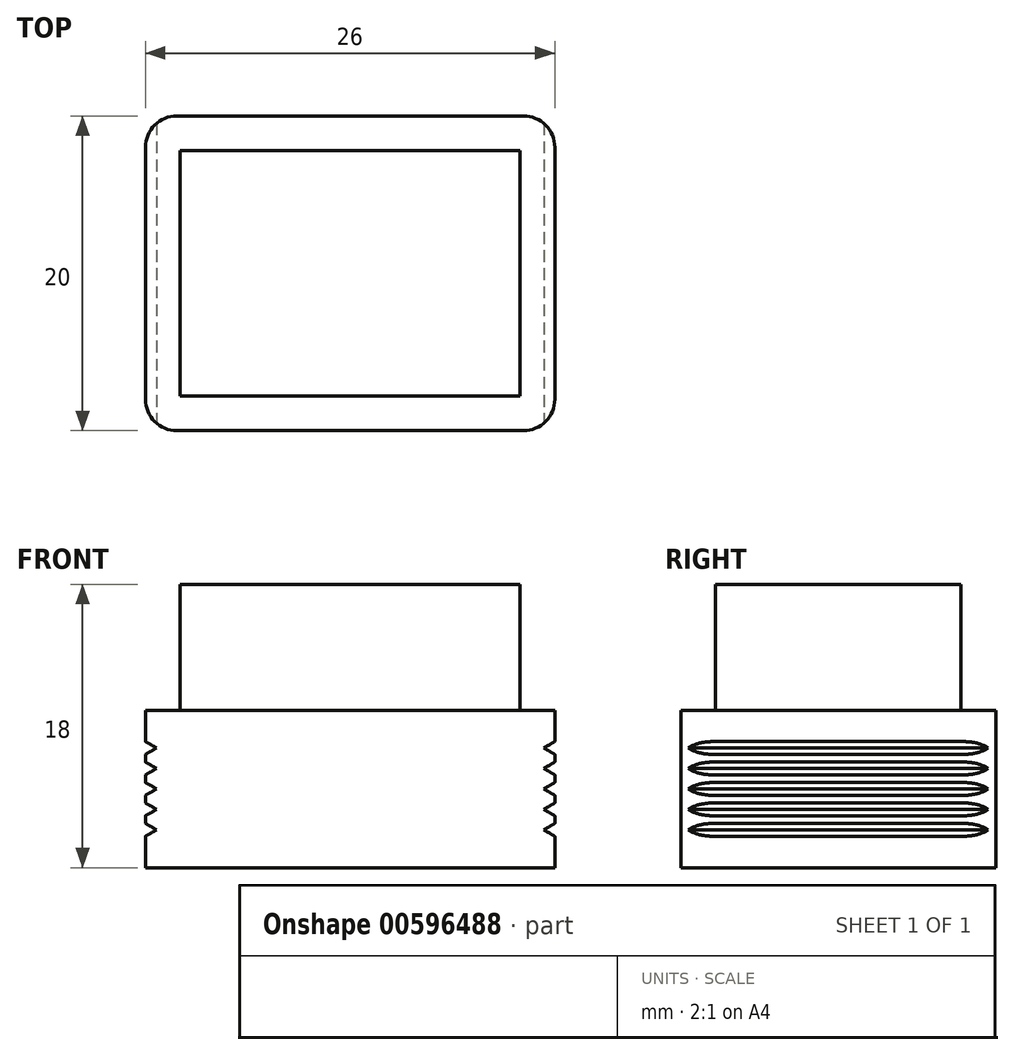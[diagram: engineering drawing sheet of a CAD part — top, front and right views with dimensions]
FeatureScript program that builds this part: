
annotation { "Feature Type Name" : "Feature", "Feature Type Description" : "" }
export const myFeature = defineFeature(function(context is Context, id is Id, definition is map)
    precondition{}
    {
        {
            var Q0;
            Q0=qCreatedBy(makeId("Top.planeOp"),FACE);
            var sketch = newSketch(context, id + "F0", { "sketchPlane" : qUnion([Q0])});
            skLineSegment(sketch, "E0.bottom", {"start": v(0, 0) * mm, "end": v(26, 0) * mm});
            skLineSegment(sketch, "E0.top", {"start": v(0, 20) * mm, "end": v(26, 20) * mm});
            skLineSegment(sketch, "E0.left", {"start": v(0, 0) * mm, "end": v(0, 20) * mm});
            skLineSegment(sketch, "E0.right", {"start": v(26, 0) * mm, "end": v(26, 20) * mm});
            skLineSegment(sketch, "E1.bottom", {"start": v(23.8, 17.8) * mm, "end": v(2.2, 17.8) * mm});
            skLineSegment(sketch, "E1.top", {"start": v(23.8, 2.2) * mm, "end": v(2.2, 2.2) * mm});
            skLineSegment(sketch, "E1.left", {"start": v(23.8, 17.8) * mm, "end": v(23.8, 2.2) * mm});
            skLineSegment(sketch, "E1.right", {"start": v(2.2, 17.8) * mm, "end": v(2.2, 2.2) * mm});
            skPoint(sketch, "E1.middle", {"position": v(13, 10) * mm});
            skPoint(sketch, "E1.middle.positionSnap0", {"position": v(13, 20) * mm});
            skPoint(sketch, "E1.middle.positionSnap1", {"position": v(0, 10) * mm});
            skPoint(sketch, "E1.centerSnap0", {"position": v(13, 20) * mm});
            skPoint(sketch, "E1.centerSnap1", {"position": v(0, 10) * mm});
            skSolve(sketch);
        }
        {
            var Q0;
            Q0=makeQuery(id+"F0.imprint","IMPRINT",FACE,{"disambiguationData":[TD([[makeQuery(id+"F0.imprint","IMPRINT",EDGE,{"derivedFrom":sQuery(id+"F0.wireOp",EDGE,"E0.bottom")}),1.0]])]});
            extrude(context, id + "F1", {"entities" : qUnion([Q0]), "depth" : 10 * mm, "offsetDistance" : 25 * mm});
        }
        {
            var Q0;
            Q0=makeQuery(id+"F0.imprint","IMPRINT",FACE,{"disambiguationData":[TD([[makeQuery(id+"F0.imprint","IMPRINT",EDGE,{"derivedFrom":sQuery(id+"F0.wireOp",EDGE,"E1.bottom")}),1.0]])]});
            extrude(context, id + "F2", {"entities" : qUnion([Q0]), "operationType" : NewBodyOperationType.ADD, "depth" : 18 * mm, "offsetDistance" : 25 * mm});
        }
        {
            var Q0;
            Q0=makeQuery(id+"F1.opExtrude","SWEPT_EDGE",EDGE,{"disambiguationData":[OSD([sQuery(id+"F0.wireOp",EDGE,"E0.bottom"),sQuery(id+"F0.wireOp",EDGE,"E0.right")])]});
            var Q1;
            Q1=makeQuery(id+"F1.opExtrude","SWEPT_EDGE",EDGE,{"disambiguationData":[OSD([sQuery(id+"F0.wireOp",EDGE,"E0.top"),sQuery(id+"F0.wireOp",EDGE,"E0.right")])]});
            var Q2;
            Q2=makeQuery(id+"F1.opExtrude","SWEPT_EDGE",EDGE,{"disambiguationData":[OSD([sQuery(id+"F0.wireOp",EDGE,"E0.top"),sQuery(id+"F0.wireOp",EDGE,"E0.left")])]});
            var Q3;
            Q3=makeQuery(id+"F1.opExtrude","SWEPT_EDGE",EDGE,{"disambiguationData":[OSD([sQuery(id+"F0.wireOp",EDGE,"E0.bottom"),sQuery(id+"F0.wireOp",EDGE,"E0.left")])]});
            fillet(context, id + "F3", {"entities" : qUnion([Q0, Q1, Q2, Q3]), "radius" : 2 * mm, "tangentPropagation" : true, "allowEdgeOverflow" : false});
        }
        {
            var Q0;
            Q0=makeQuery(id+"F1.opExtrude","SWEPT_FACE",FACE,{"disambiguationData":[OSD([sQuery(id+"F0.wireOp",EDGE,"E0.bottom")])]});
            var sketch = newSketch(context, id + "F4", { "sketchPlane" : qUnion([Q0])});
            skLineSegment(sketch, "E2.0", {"start": v(0, 0) * mm, "end": v(0, 10) * mm});
            skLineSegment(sketch, "E3.0", {"start": v(26, 10) * mm, "end": v(26, 0) * mm});
            skLineSegment(sketch, "E4", {"start": v(0, 5) * mm, "end": v(26, 5) * mm, "construction": true});
            skLineSegment(sketch, "E5", {"start": v(13, 10) * mm, "end": v(13, 0) * mm, "construction": true});
            skCircle(sketch, "E6.cCircle", {"center": v(0, 5) * mm, "radius": 0.35 * mm, "construction": true});
            skLineSegment(sketch, "E6.0", {"start": v(-0.35, 4.4) * mm, "end": v(-0.35, 5.6) * mm});
            skLineSegment(sketch, "E6.1", {"start": v(-0.35, 5.6) * mm, "end": v(0.7, 5) * mm});
            skLineSegment(sketch, "E6.2", {"start": v(0.7, 5) * mm, "end": v(-0.35, 4.4) * mm});
            skPoint(sketch, "E6.0.midPoint", {"position": v(-0.35, 5) * mm});
            skPoint(sketch, "E7.0.1.0", {"position": v(-0.35, 6.3) * mm});
            skLineSegment(sketch, "E7.0.1.1", {"start": v(0.7, 6.3) * mm, "end": v(-0.35, 5.7) * mm});
            skLineSegment(sketch, "E7.0.1.2", {"start": v(-0.35, 6.9) * mm, "end": v(0.7, 6.3) * mm});
            skLineSegment(sketch, "E7.0.1.3", {"start": v(-0.35, 5.7) * mm, "end": v(-0.35, 6.9) * mm});
            skCircle(sketch, "E7.0.1.4", {"center": v(0, 6.3) * mm, "radius": 0.35 * mm, "construction": true});
            skPoint(sketch, "E7.0.2.0", {"position": v(-0.35, 7.6) * mm});
            skLineSegment(sketch, "E7.0.2.1", {"start": v(0.7, 7.6) * mm, "end": v(-0.35, 7) * mm});
            skLineSegment(sketch, "E7.0.2.2", {"start": v(-0.35, 8.2) * mm, "end": v(0.7, 7.6) * mm});
            skLineSegment(sketch, "E7.0.2.3", {"start": v(-0.35, 7) * mm, "end": v(-0.35, 8.2) * mm});
            skCircle(sketch, "E7.0.2.4", {"center": v(0, 7.6) * mm, "radius": 0.35 * mm, "construction": true});
            skLineSegment(sketch, "E7.direction1", {"start": v(-0.35, 5) * mm, "end": v(3.53, 5) * mm, "construction": true});
            skLineSegment(sketch, "E7.direction2", {"start": v(-0.35, 5) * mm, "end": v(-0.35, 6.3) * mm, "construction": true});
            skLineSegment(sketch, "E8.MirrorCS", {"start": v(0.7, 2.4) * mm, "end": v(-0.35, 3) * mm});
            skCircle(sketch, "E9.MirrorC", {"center": v(0, 3.7) * mm, "radius": 0.35 * mm, "construction": true});
            skPoint(sketch, "E10.MirrorP", {"position": v(-0.35, 2.4) * mm});
            skCircle(sketch, "E11.MirrorC", {"center": v(0, 2.4) * mm, "radius": 0.35 * mm, "construction": true});
            skLineSegment(sketch, "E12.MirrorCS", {"start": v(-0.35, 3) * mm, "end": v(-0.35, 1.8) * mm});
            skLineSegment(sketch, "E13.MirrorCS", {"start": v(-0.35, 1.8) * mm, "end": v(0.7, 2.4) * mm});
            skLineSegment(sketch, "E14.MirrorCS", {"start": v(0.7, 3.7) * mm, "end": v(-0.35, 4.3) * mm});
            skLineSegment(sketch, "E15.MirrorCS", {"start": v(-0.35, 4.3) * mm, "end": v(-0.35, 3.1) * mm});
            skLineSegment(sketch, "E16.MirrorCS", {"start": v(-0.35, 3.1) * mm, "end": v(0.7, 3.7) * mm});
            skPoint(sketch, "E17.MirrorP", {"position": v(-0.35, 3.7) * mm});
            skLineSegment(sketch, "E18.MirrorCS", {"start": v(-0.35, 5.6) * mm, "end": v(-0.35, 4.4) * mm});
            skLineSegment(sketch, "E19.MirrorCS", {"start": v(-0.35, 5) * mm, "end": v(-0.35, 3.7) * mm, "construction": true});
            skLineSegment(sketch, "E20.MirrorCS", {"start": v(0.7, 5) * mm, "end": v(-0.35, 5.6) * mm});
            skLineSegment(sketch, "E21.MirrorCS", {"start": v(-0.35, 4.4) * mm, "end": v(0.7, 5) * mm});
            skLineSegment(sketch, "E22.MirrorCS", {"start": v(26.35, 5.6) * mm, "end": v(26.35, 4.4) * mm});
            skLineSegment(sketch, "E23.MirrorCS", {"start": v(26.35, 4.4) * mm, "end": v(26.35, 5.6) * mm});
            skLineSegment(sketch, "E24.MirrorCS", {"start": v(26.35, 3) * mm, "end": v(26.35, 1.8) * mm});
            skLineSegment(sketch, "E25.MirrorCS", {"start": v(26.35, 4.3) * mm, "end": v(26.35, 3.1) * mm});
            skLineSegment(sketch, "E26.MirrorCS", {"start": v(26.35, 5.7) * mm, "end": v(26.35, 6.9) * mm});
            skLineSegment(sketch, "E27.MirrorCS", {"start": v(26.35, 5) * mm, "end": v(26.35, 6.3) * mm, "construction": true});
            skLineSegment(sketch, "E28.MirrorCS", {"start": v(26.35, 7) * mm, "end": v(26.35, 8.2) * mm});
            skLineSegment(sketch, "E29.MirrorCS", {"start": v(26.35, 5) * mm, "end": v(26.35, 3.7) * mm, "construction": true});
            skLineSegment(sketch, "E30.MirrorCS", {"start": v(25.3, 6.3) * mm, "end": v(26.35, 5.7) * mm});
            skCircle(sketch, "E31.MirrorC", {"center": v(26, 2.4) * mm, "radius": 0.35 * mm, "construction": true});
            skPoint(sketch, "E32.MirrorP", {"position": v(26.35, 6.3) * mm});
            skPoint(sketch, "E33.MirrorP", {"position": v(26.35, 5) * mm});
            skPoint(sketch, "E34.MirrorP", {"position": v(26.35, 2.4) * mm});
            skCircle(sketch, "E35.MirrorC", {"center": v(26, 7.6) * mm, "radius": 0.35 * mm, "construction": true});
            skLineSegment(sketch, "E36.MirrorCS", {"start": v(26.35, 4.4) * mm, "end": v(25.3, 5) * mm});
            skLineSegment(sketch, "E37.MirrorCS", {"start": v(25.3, 2.4) * mm, "end": v(26.35, 3) * mm});
            skLineSegment(sketch, "E38.MirrorCS", {"start": v(25.3, 3.7) * mm, "end": v(26.35, 4.3) * mm});
            skCircle(sketch, "E39.MirrorC", {"center": v(26, 6.3) * mm, "radius": 0.35 * mm, "construction": true});
            skCircle(sketch, "E40.MirrorC", {"center": v(26, 5) * mm, "radius": 0.35 * mm, "construction": true});
            skLineSegment(sketch, "E41.MirrorCS", {"start": v(26.35, 1.8) * mm, "end": v(25.3, 2.4) * mm});
            skCircle(sketch, "E42.MirrorC", {"center": v(26, 3.7) * mm, "radius": 0.35 * mm, "construction": true});
            skPoint(sketch, "E43.MirrorP", {"position": v(26.35, 3.7) * mm});
            skLineSegment(sketch, "E44.MirrorCS", {"start": v(25.3, 7.6) * mm, "end": v(26.35, 7) * mm});
            skLineSegment(sketch, "E45.MirrorCS", {"start": v(26.35, 3.1) * mm, "end": v(25.3, 3.7) * mm});
            skPoint(sketch, "E46.MirrorP", {"position": v(26.35, 7.6) * mm});
            skLineSegment(sketch, "E47.MirrorCS", {"start": v(26.35, 6.9) * mm, "end": v(25.3, 6.3) * mm});
            skLineSegment(sketch, "E48.MirrorCS", {"start": v(25.3, 5) * mm, "end": v(26.35, 5.6) * mm});
            skLineSegment(sketch, "E49.MirrorCS", {"start": v(26.35, 5.6) * mm, "end": v(25.3, 5) * mm});
            skLineSegment(sketch, "E50.MirrorCS", {"start": v(25.3, 5) * mm, "end": v(26.35, 4.4) * mm});
            skLineSegment(sketch, "E51.MirrorCS", {"start": v(26.35, 8.2) * mm, "end": v(25.3, 7.6) * mm});
            skSolve(sketch);
        }
        {
            var Q0;
            {var subQ0=sQuery(id+"F4.wireOp",EDGE,"E37.MirrorCS");var subQ1=sQuery(id+"F4.wireOp",EDGE,"E3.0");var subQ2=makeQuery(id+"F4.imprint","INTERSECT",VERTEX,{"derivedFrom":[subQ1,subQ0]});Q0=makeQuery(id+"F4.imprint","IMPRINT",FACE,{"disambiguationData":[TD([[makeQuery(id+"F4.imprint","IMPRINT",EDGE,{"disambiguationData":[TD([[subQ2,-1.0]])],"derivedFrom":subQ1}),-1.0]])]});}
            var Q1;
            {var subQ0=sQuery(id+"F4.wireOp",EDGE,"E38.MirrorCS");var subQ1=sQuery(id+"F4.wireOp",EDGE,"E3.0");var subQ2=makeQuery(id+"F4.imprint","INTERSECT",VERTEX,{"derivedFrom":[subQ1,subQ0]});Q1=makeQuery(id+"F4.imprint","IMPRINT",FACE,{"disambiguationData":[TD([[makeQuery(id+"F4.imprint","IMPRINT",EDGE,{"disambiguationData":[TD([[subQ2,-1.0]])],"derivedFrom":subQ1}),-1.0]])]});}
            var Q2;
            {var subQ5=sQuery(id+"F4.wireOp",EDGE,"E24.MirrorCS");Q2=makeQuery(id+"F4.imprint","IMPRINT",FACE,{"disambiguationData":[TD([[makeQuery(id+"F4.imprint","IMPRINT",EDGE,{"derivedFrom":subQ5}),-1.0]])]});}
            var Q3;
            {var subQ5=sQuery(id+"F4.wireOp",EDGE,"E25.MirrorCS");Q3=makeQuery(id+"F4.imprint","IMPRINT",FACE,{"disambiguationData":[TD([[makeQuery(id+"F4.imprint","IMPRINT",EDGE,{"derivedFrom":subQ5}),-1.0]])]});}
            var Q4;
            {var subQ5=sQuery(id+"F4.wireOp",EDGE,"E22.MirrorCS");Q4=makeQuery(id+"F4.imprint","IMPRINT",FACE,{"disambiguationData":[TD([[makeQuery(id+"F4.imprint","IMPRINT",EDGE,{"derivedFrom":subQ5}),-1.0]])]});}
            var Q5;
            {var subQ0=sQuery(id+"F4.wireOp",EDGE,"E49.MirrorCS");var subQ1=sQuery(id+"F4.wireOp",EDGE,"E3.0");var subQ2=makeQuery(id+"F4.imprint","INTERSECT",VERTEX,{"derivedFrom":[subQ1,subQ0]});Q5=makeQuery(id+"F4.imprint","IMPRINT",FACE,{"disambiguationData":[TD([[makeQuery(id+"F4.imprint","IMPRINT",EDGE,{"disambiguationData":[TD([[subQ2,-1.0]])],"derivedFrom":subQ1}),-1.0]])]});}
            var Q6;
            {var subQ5=sQuery(id+"F4.wireOp",EDGE,"E26.MirrorCS");Q6=makeQuery(id+"F4.imprint","IMPRINT",FACE,{"disambiguationData":[TD([[makeQuery(id+"F4.imprint","IMPRINT",EDGE,{"derivedFrom":subQ5}),1.0]])]});}
            var Q7;
            {var subQ0=sQuery(id+"F4.wireOp",EDGE,"E30.MirrorCS");var subQ1=sQuery(id+"F4.wireOp",EDGE,"E3.0");var subQ2=makeQuery(id+"F4.imprint","INTERSECT",VERTEX,{"derivedFrom":[subQ1,subQ0]});Q7=makeQuery(id+"F4.imprint","IMPRINT",FACE,{"disambiguationData":[TD([[makeQuery(id+"F4.imprint","IMPRINT",EDGE,{"disambiguationData":[TD([[subQ2,1.0]])],"derivedFrom":subQ1}),-1.0]])]});}
            var Q8;
            {var subQ0=sQuery(id+"F4.wireOp",EDGE,"E44.MirrorCS");var subQ1=sQuery(id+"F4.wireOp",EDGE,"E3.0");var subQ2=makeQuery(id+"F4.imprint","INTERSECT",VERTEX,{"derivedFrom":[subQ1,subQ0]});Q8=makeQuery(id+"F4.imprint","IMPRINT",FACE,{"disambiguationData":[TD([[makeQuery(id+"F4.imprint","IMPRINT",EDGE,{"disambiguationData":[TD([[subQ2,1.0]])],"derivedFrom":subQ1}),-1.0]])]});}
            var Q9;
            {var subQ5=sQuery(id+"F4.wireOp",EDGE,"E28.MirrorCS");Q9=makeQuery(id+"F4.imprint","IMPRINT",FACE,{"disambiguationData":[TD([[makeQuery(id+"F4.imprint","IMPRINT",EDGE,{"derivedFrom":subQ5}),1.0]])]});}
            var Q10;
            {var subQ0=sQuery(id+"F4.wireOp",EDGE,"E7.0.2.2");var subQ1=sQuery(id+"F4.wireOp",EDGE,"E2.0");var subQ2=makeQuery(id+"F4.imprint","INTERSECT",VERTEX,{"derivedFrom":[subQ1,subQ0]});Q10=makeQuery(id+"F4.imprint","IMPRINT",FACE,{"disambiguationData":[TD([[makeQuery(id+"F4.imprint","IMPRINT",EDGE,{"disambiguationData":[TD([[subQ2,1.0]])],"derivedFrom":subQ1}),-1.0]])]});}
            var Q11;
            {var subQ0=sQuery(id+"F4.wireOp",EDGE,"E7.0.1.1");var subQ1=sQuery(id+"F4.wireOp",EDGE,"E2.0");var subQ2=makeQuery(id+"F4.imprint","INTERSECT",VERTEX,{"derivedFrom":[subQ1,subQ0]});Q11=makeQuery(id+"F4.imprint","IMPRINT",FACE,{"disambiguationData":[TD([[makeQuery(id+"F4.imprint","IMPRINT",EDGE,{"disambiguationData":[TD([[subQ2,-1.0]])],"derivedFrom":subQ1}),-1.0]])]});}
            var Q12;
            {var subQ0=sQuery(id+"F4.wireOp",EDGE,"E6.2");var subQ1=sQuery(id+"F4.wireOp",EDGE,"E2.0");var subQ2=makeQuery(id+"F4.imprint","INTERSECT",VERTEX,{"derivedFrom":[subQ1,subQ0]});Q12=makeQuery(id+"F4.imprint","IMPRINT",FACE,{"disambiguationData":[TD([[makeQuery(id+"F4.imprint","IMPRINT",EDGE,{"disambiguationData":[TD([[subQ2,-1.0]])],"derivedFrom":subQ1}),-1.0]])]});}
            var Q13;
            {var subQ0=sQuery(id+"F4.wireOp",EDGE,"E16.MirrorCS");var subQ1=sQuery(id+"F4.wireOp",EDGE,"E2.0");var subQ2=makeQuery(id+"F4.imprint","INTERSECT",VERTEX,{"derivedFrom":[subQ1,subQ0]});Q13=makeQuery(id+"F4.imprint","IMPRINT",FACE,{"disambiguationData":[TD([[makeQuery(id+"F4.imprint","IMPRINT",EDGE,{"disambiguationData":[TD([[subQ2,-1.0]])],"derivedFrom":subQ1}),-1.0]])]});}
            var Q14;
            {var subQ5=sQuery(id+"F4.wireOp",EDGE,"E7.0.2.3");Q14=makeQuery(id+"F4.imprint","IMPRINT",FACE,{"disambiguationData":[TD([[makeQuery(id+"F4.imprint","IMPRINT",EDGE,{"derivedFrom":subQ5}),-1.0]])]});}
            var Q15;
            {var subQ5=sQuery(id+"F4.wireOp",EDGE,"E7.0.1.3");Q15=makeQuery(id+"F4.imprint","IMPRINT",FACE,{"disambiguationData":[TD([[makeQuery(id+"F4.imprint","IMPRINT",EDGE,{"derivedFrom":subQ5}),-1.0]])]});}
            var Q16;
            {var subQ0=sQuery(id+"F4.wireOp",EDGE,"E13.MirrorCS");var subQ1=sQuery(id+"F4.wireOp",EDGE,"E2.0");var subQ2=makeQuery(id+"F4.imprint","INTERSECT",VERTEX,{"derivedFrom":[subQ1,subQ0]});Q16=makeQuery(id+"F4.imprint","IMPRINT",FACE,{"disambiguationData":[TD([[makeQuery(id+"F4.imprint","IMPRINT",EDGE,{"disambiguationData":[TD([[subQ2,-1.0]])],"derivedFrom":subQ1}),-1.0]])]});}
            var Q17;
            {var subQ5=sQuery(id+"F4.wireOp",EDGE,"E18.MirrorCS");Q17=makeQuery(id+"F4.imprint","IMPRINT",FACE,{"disambiguationData":[TD([[makeQuery(id+"F4.imprint","IMPRINT",EDGE,{"derivedFrom":subQ5}),1.0]])]});}
            var Q18;
            {var subQ5=sQuery(id+"F4.wireOp",EDGE,"E15.MirrorCS");Q18=makeQuery(id+"F4.imprint","IMPRINT",FACE,{"disambiguationData":[TD([[makeQuery(id+"F4.imprint","IMPRINT",EDGE,{"derivedFrom":subQ5}),1.0]])]});}
            var Q19;
            {var subQ5=sQuery(id+"F4.wireOp",EDGE,"E12.MirrorCS");Q19=makeQuery(id+"F4.imprint","IMPRINT",FACE,{"disambiguationData":[TD([[makeQuery(id+"F4.imprint","IMPRINT",EDGE,{"derivedFrom":subQ5}),1.0]])]});}
            var Q20;
            Q20=makeQuery(id+"F1.opExtrude","SWEPT_FACE",FACE,{"disambiguationData":[OSD([sQuery(id+"F0.wireOp",EDGE,"E0.top")])]});
            extrude(context, id + "F5", {"entities" : qUnion([Q0, Q1, Q2, Q3, Q4, Q5, Q6, Q7, Q8, Q9, Q10, Q11, Q12, Q13, Q14, Q15, Q16, Q17, Q18, Q19]), "operationType" : NewBodyOperationType.REMOVE, "endBound" : BoundingType.UP_TO_SURFACE, "oppositeDirection" : true, "depth" : 25 * mm, "endBoundEntityFace" : qUnion([Q20]), "offsetDistance" : 25 * mm});
        }
    });
